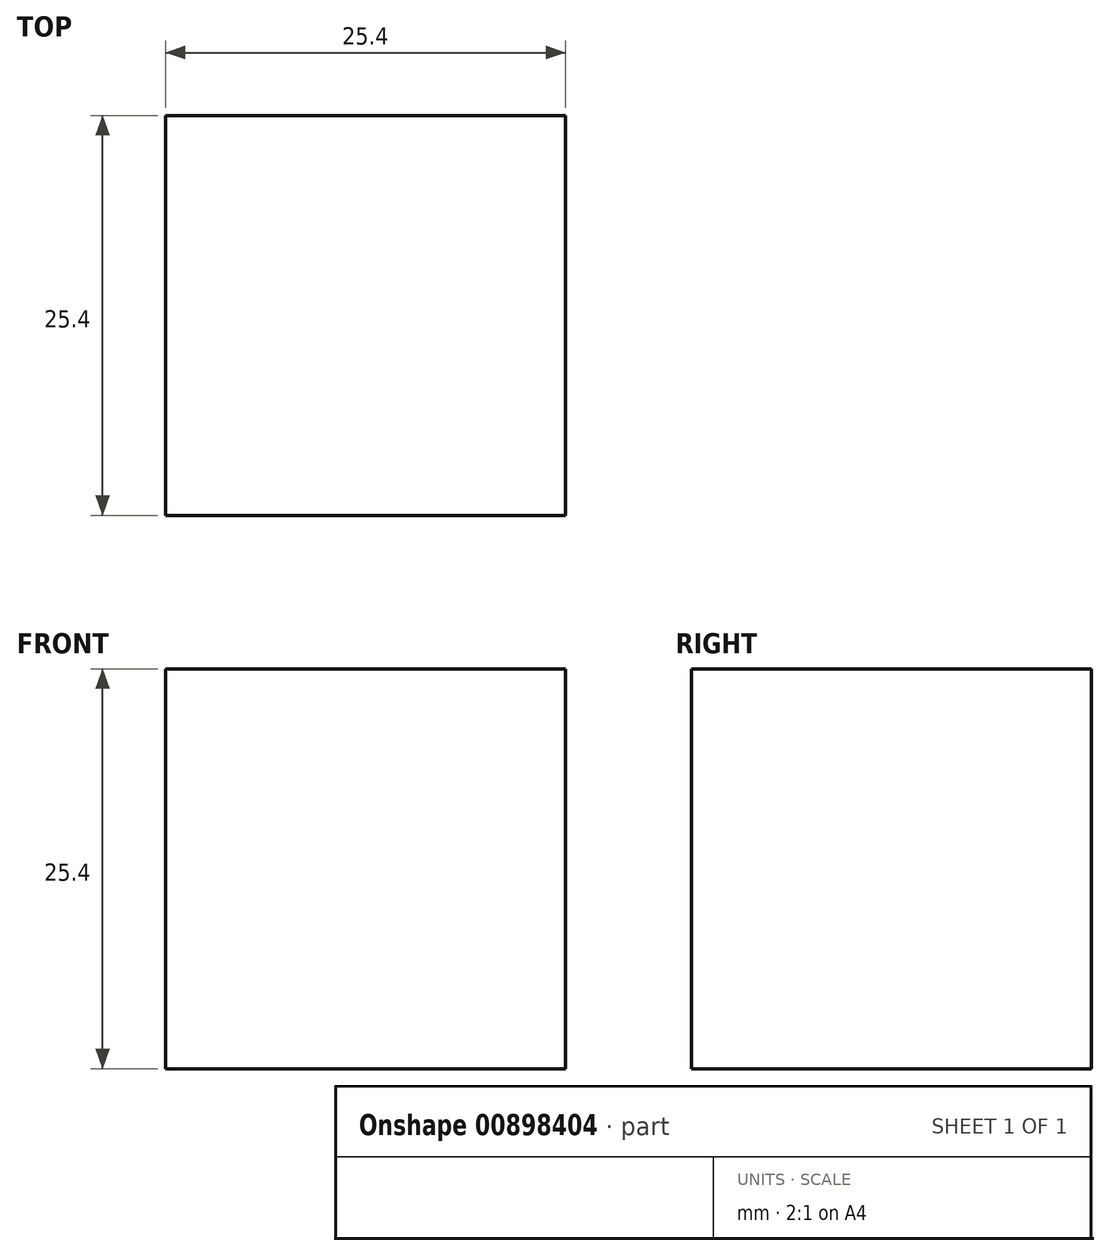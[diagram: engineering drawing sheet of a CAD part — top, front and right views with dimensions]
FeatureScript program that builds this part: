
annotation { "Feature Type Name" : "Feature", "Feature Type Description" : "" }
export const myFeature = defineFeature(function(context is Context, id is Id, definition is map)
    precondition{}
    {
        {
            var Q0;
            Q0=qCreatedBy(makeId("Top.planeOp"),FACE);
            var sketch = newSketch(context, id + "F0", { "sketchPlane" : qUnion([Q0])});
            skLineSegment(sketch, "E0.bottom", {"start": v(0, 0) * mm, "end": v(25.4, 0) * mm});
            skLineSegment(sketch, "E0.top", {"start": v(0, 25.4) * mm, "end": v(25.4, 25.4) * mm});
            skLineSegment(sketch, "E0.left", {"start": v(0, 0) * mm, "end": v(0, 25.4) * mm});
            skLineSegment(sketch, "E0.right", {"start": v(25.4, 0) * mm, "end": v(25.4, 25.4) * mm});
            skSolve(sketch);
        }
        {
            var Q0;
            Q0=makeQuery(id+"F0.imprint","IMPRINT",FACE,{"disambiguationData":[TD([[makeQuery(id+"F0.imprint","IMPRINT",EDGE,{"derivedFrom":sQuery(id+"F0.wireOp",EDGE,"E0.bottom")}),1.0]])]});
            extrude(context, id + "F1", {"entities" : qUnion([Q0]), "depth" : 25.4 * mm, "offsetDistance" : 25.4 * mm});
        }
    });
